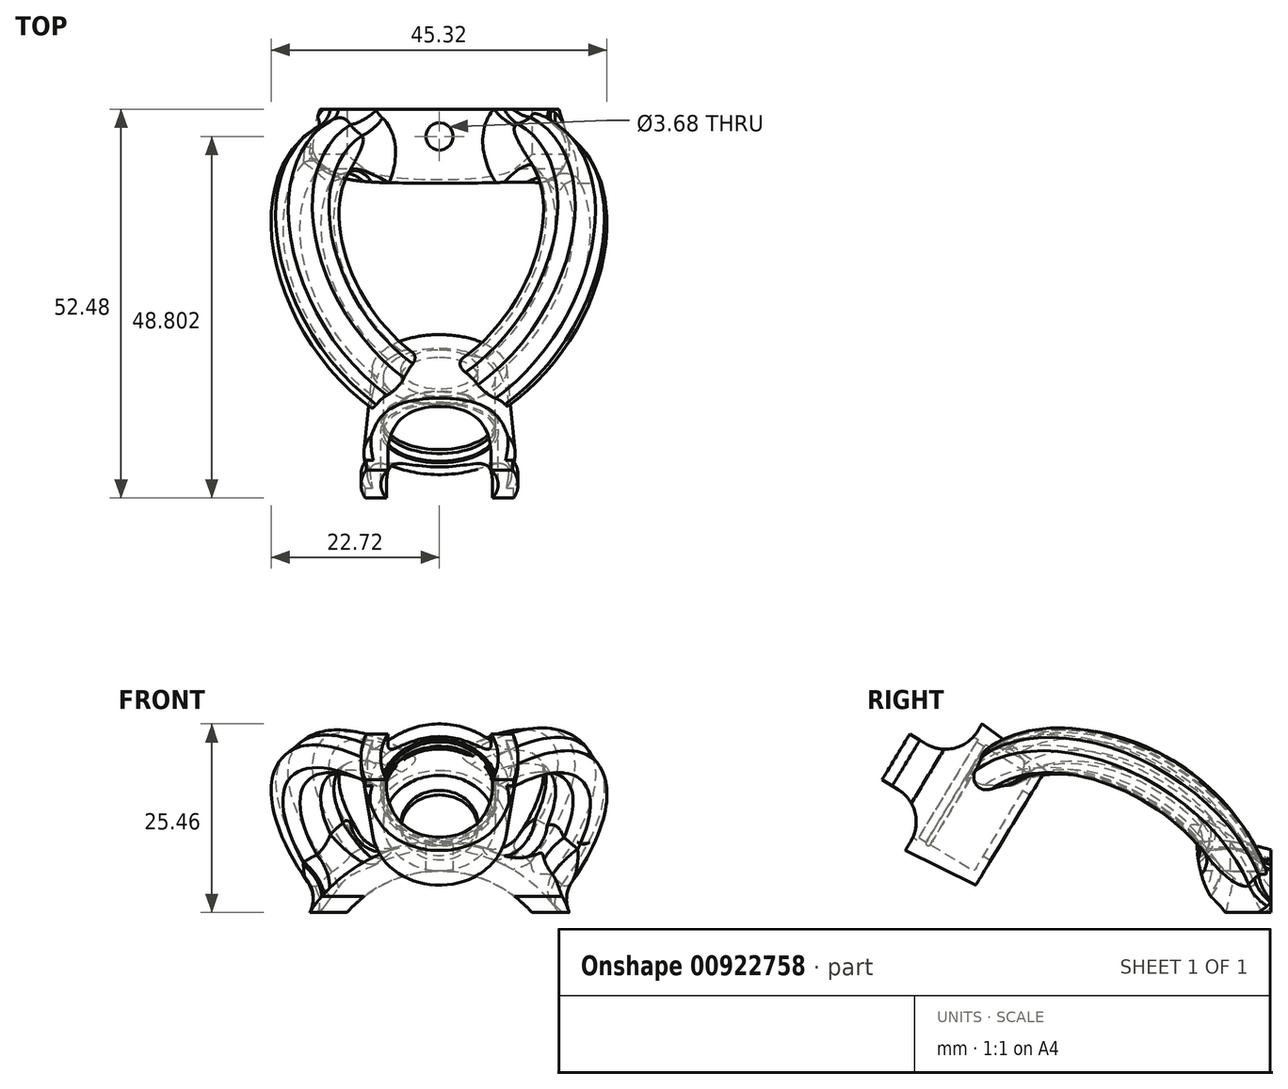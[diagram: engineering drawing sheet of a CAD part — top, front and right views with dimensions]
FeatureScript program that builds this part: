
annotation { "Feature Type Name" : "Feature", "Feature Type Description" : "" }
export const myFeature = defineFeature(function(context is Context, id is Id, definition is map)
    precondition{}
    {
        {
            var Q0;
            Q0=qCreatedBy(makeId("Right.planeOp"),FACE);
            var sketch = newSketch(context, id + "F0", { "sketchPlane" : qUnion([Q0])});
            skLineSegment(sketch, "E0", {"start": v(0, 0) * mm, "end": v(15.88, 0) * mm, "construction": true});
            skLineSegment(sketch, "E1", {"start": v(0, 0) * mm, "end": v(0, 16.68) * mm, "construction": true});
            skLineSegment(sketch, "E2", {"start": v(0, 0) * mm, "end": v(0, -16.68) * mm, "construction": true});
            skLineSegment(sketch, "E3", {"start": v(0, 16.68) * mm, "end": v(-2.38, 16.68) * mm});
            skLineSegment(sketch, "E4", {"start": v(-2.38, 16.68) * mm, "end": v(-2.38, 19.06) * mm});
            skLineSegment(sketch, "E5", {"start": v(-2.38, 19.06) * mm, "end": v(0, 19.06) * mm, "construction": true});
            skLineSegment(sketch, "E6", {"start": v(0, 19.06) * mm, "end": v(0, 16.68) * mm, "construction": true});
            skPoint(sketch, "E7", {"position": v(-12.7, 16.68) * mm});
            skLineSegment(sketch, "E8", {"start": v(-2.38, 16.68) * mm, "end": v(-12.7, 16.68) * mm});
            skLineSegment(sketch, "E9", {"start": v(-11.9, 18.96) * mm, "end": v(-11.9, 20.55) * mm});
            skPoint(sketch, "E10", {"position": v(-7.14, 20.64) * mm});
            skFitSpline(sketch, "E11", {"points": [v(0, 19.06) * mm, v(-7.14, 20.64) * mm, v(-11.9, 20.55) * mm], "startDerivative": vector(-14.9, 3.6) * mm, "endDerivative": vector(-10.3, -0.6) * mm});
            skLineSegment(sketch, "E12", {"start": v(0, 0) * mm, "end": v(-3.87, -6.39) * mm, "construction": true});
            skLineSegment(sketch, "E13", {"start": v(-3.87, -6.39) * mm, "end": v(-41.99, 16.68) * mm, "construction": true});
            skLineSegment(sketch, "E14", {"start": v(-12.7, 16.68) * mm, "end": v(-47.78, 16.68) * mm, "construction": true});
            skLineSegment(sketch, "E15", {"start": v(0, 0) * mm, "end": v(3.94, 6.52) * mm, "construction": true});
            skLineSegment(sketch, "E16", {"start": v(3.94, 6.52) * mm, "end": v(-34.18, 29.58) * mm, "construction": true});
            skLineSegment(sketch, "E17", {"start": v(-34.18, 29.58) * mm, "end": v(-41.99, 16.68) * mm, "construction": true});
            skLineSegment(sketch, "E18", {"start": v(-34.18, 29.58) * mm, "end": v(-58.62, 44.38) * mm, "construction": true});
            skLineSegment(sketch, "E19", {"start": v(-58.62, 44.38) * mm, "end": v(-66.35, 31.6) * mm, "construction": true});
            skLineSegment(sketch, "E20", {"start": v(-66.35, 31.6) * mm, "end": v(-41.99, 16.68) * mm, "construction": true});
            skLineSegment(sketch, "E21", {"start": v(-34.18, 29.58) * mm, "end": v(-35.4, 27.55) * mm});
            skLineSegment(sketch, "E22", {"start": v(-35.4, 27.55) * mm, "end": v(-34.39, 26.93) * mm});
            skLineSegment(sketch, "E23", {"start": v(-34.18, 29.58) * mm, "end": v(-41.65, 34.1) * mm});
            skLineSegment(sketch, "E24", {"start": v(-41.65, 34.1) * mm, "end": v(-40.86, 35.4) * mm});
            skLineSegment(sketch, "E25", {"start": v(-40.86, 35.4) * mm, "end": v(-32.37, 30.27) * mm});
            skLineSegment(sketch, "E26", {"start": v(-34.39, 26.93) * mm, "end": v(-32.37, 30.27) * mm});
            skLineSegment(sketch, "E27", {"start": v(-40.86, 35.4) * mm, "end": v(-47.92, 39.68) * mm});
            skLineSegment(sketch, "E28", {"start": v(-47.92, 39.68) * mm, "end": v(-48.51, 38.7) * mm});
            skLineSegment(sketch, "E29", {"start": v(-48.51, 38.7) * mm, "end": v(-41.45, 34.43) * mm});
            skLineSegment(sketch, "E30", {"start": v(-38.08, 23.13) * mm, "end": v(-42, 25.5) * mm, "construction": true});
            skLineSegment(sketch, "E31", {"start": v(-11.9, 18.96) * mm, "end": v(-7.14, 18.96) * mm});
            skLineSegment(sketch, "E32", {"start": v(-7.14, 18.96) * mm, "end": v(-4.16, 16.68) * mm});
            skLineSegment(sketch, "E33", {"start": v(-11.9, 18.96) * mm, "end": v(-11.9, 16.68) * mm});
            skLineSegment(sketch, "E34", {"start": v(-2.38, 19.06) * mm, "end": v(-2.38, 19.66) * mm});
            skLineSegment(sketch, "E35", {"start": v(-1.93, 16.68) * mm, "end": v(-1.93, 19.54) * mm});
            skLineSegment(sketch, "E36", {"start": v(-47.92, 39.68) * mm, "end": v(-47.13, 40.98) * mm});
            skLineSegment(sketch, "E37", {"start": v(-47.13, 40.98) * mm, "end": v(-45.77, 40.16) * mm});
            skLineSegment(sketch, "E38", {"start": v(-45.77, 40.16) * mm, "end": v(-46.56, 38.86) * mm});
            skCircle(sketch, "E39", {"center": v(-40.34, 33.31) * mm, "radius": 0.32 * mm});
            skLineSegment(sketch, "E40", {"start": v(-32.37, 30.27) * mm, "end": v(-43.04, 38.06) * mm});
            skLineSegment(sketch, "E41", {"start": v(-43.04, 38.06) * mm, "end": v(-43.63, 37.08) * mm});
            skLineSegment(sketch, "E42", {"start": v(-43.04, 38.06) * mm, "end": v(-46.23, 39.4) * mm});
            skSolve(sketch);
        }
        {
            var Q0;
            {var subQ0=sQuery(id+"F0.wireOp",EDGE,"41GGEf58-UM0G-m7PR-pCRU-CCuLjlQgezV2");Q0=makeQuery(id+"F0.imprint","IMPRINT",FACE,{"disambiguationData":[TD([[makeQuery(id+"F0.imprint","IMPRINT",EDGE,{"derivedFrom":subQ0}),-1.0]])]});}
            var Q1;
            {var subQ2=sQuery(id+"F0.wireOp",EDGE,"E4");Q1=makeQuery(id+"F0.imprint","IMPRINT",FACE,{"disambiguationData":[TD([[makeQuery(id+"F0.imprint","IMPRINT",EDGE,{"derivedFrom":subQ2}),1.0]])]});}
            var Q2;
            Q2=makeQuery(id+"F0.imprint","IMPRINT",FACE,{"disambiguationData":[TD([[makeQuery(id+"F0.imprint","IMPRINT",EDGE,{"derivedFrom":sQuery(id+"F0.wireOp",EDGE,"E3")}),-1.0]])]});
            var Q3;
            Q3=makeQuery(id+"F0.imprint","IMPRINT",FACE,{"disambiguationData":[TD([[makeQuery(id+"F0.imprint","IMPRINT",EDGE,{"derivedFrom":sQuery(id+"F0.wireOp",EDGE,"E31")}),-1.0]])]});
            var Q4;
            Q4=sQuery(id+"F0.wireOp",EDGE,"E0");
            revolve(context, id + "F1", {"surfaceOperationType" : NewSurfaceOperationType.NEW, "entities" : qUnion([Q0, Q1, Q2, Q3]), "axis" : qUnion([Q4]), "revolveType" : RevolveType.SYMMETRIC, "angle" : 210 * degree});
        }
        {
            var Q0;
            Q0=makeQuery(id+"F0.imprint","IMPRINT",FACE,{"disambiguationData":[TD([[makeQuery(id+"F0.imprint","IMPRINT",EDGE,{"derivedFrom":sQuery(id+"F0.wireOp",EDGE,"E21")}),1.0]])]});
            var Q1;
            {var subQ0=sQuery(id+"F0.wireOp",EDGE,"E27");Q1=makeQuery(id+"F0.imprint","IMPRINT",FACE,{"disambiguationData":[TD([[makeQuery(id+"F0.imprint","IMPRINT",EDGE,{"derivedFrom":subQ0}),1.0]])]});}
            var Q2;
            {var subQ0=sQuery(id+"F0.wireOp",EDGE,"E36");Q2=makeQuery(id+"F0.imprint","IMPRINT",FACE,{"disambiguationData":[TD([[makeQuery(id+"F0.imprint","IMPRINT",EDGE,{"derivedFrom":subQ0}),-1.0]])]});}
            var Q3;
            {var subQ0=sQuery(id+"F0.wireOp",EDGE,"E39");var subQ1=sQuery(id+"F0.wireOp",EDGE,"E23");var subQ2=makeQuery(id+"F0.imprint","INTERSECT",VERTEX,{"disambiguationData":[OD(0.0)],"derivedFrom":[subQ1,subQ0]});Q3=makeQuery(id+"F0.imprint","IMPRINT",FACE,{"disambiguationData":[TD([[makeQuery(id+"F0.imprint","IMPRINT",EDGE,{"disambiguationData":[TD([[subQ2,-1.0]])],"derivedFrom":subQ1}),-1.0]])]});}
            var Q4;
            {var subQ0=sQuery(id+"F0.wireOp",EDGE,"E39");var subQ1=sQuery(id+"F0.wireOp",EDGE,"E23");var subQ2=makeQuery(id+"F0.imprint","INTERSECT",VERTEX,{"disambiguationData":[OD(0.0)],"derivedFrom":[subQ1,subQ0]});Q4=makeQuery(id+"F0.imprint","IMPRINT",FACE,{"disambiguationData":[TD([[makeQuery(id+"F0.imprint","IMPRINT",EDGE,{"disambiguationData":[TD([[subQ2,-1.0]])],"derivedFrom":subQ1}),1.0]])]});}
            var Q5;
            {var subQ0=sQuery(id+"F0.wireOp",EDGE,"E25");Q5=makeQuery(id+"F0.imprint","IMPRINT",FACE,{"disambiguationData":[TD([[makeQuery(id+"F0.imprint","IMPRINT",EDGE,{"derivedFrom":subQ0}),1.0]])]});}
            var Q6;
            {var subQ3=sQuery(id+"F0.wireOp",EDGE,"E41");Q6=makeQuery(id+"F0.imprint","IMPRINT",FACE,{"disambiguationData":[TD([[makeQuery(id+"F0.imprint","IMPRINT",EDGE,{"derivedFrom":subQ3}),-1.0]])]});}
            var Q7;
            Q7=sQuery(id+"F0.wireOp",EDGE,"E30");
            revolve(context, id + "F2", {"operationType" : NewBodyOperationType.ADD, "surfaceOperationType" : NewSurfaceOperationType.NEW, "entities" : qUnion([Q0, Q1, Q2, Q3, Q4, Q5, Q6]), "axis" : qUnion([Q7]), "revolveType" : RevolveType.FULL});
        }
        {
            var Q0;
            Q0=makeQuery(id+"F2.opRevolve","SWEPT_FACE",FACE,{"disambiguationData":[OSD([sQuery(id+"F0.wireOp",EDGE,"E28")])]});
            var sketch = newSketch(context, id + "F3", { "sketchPlane" : qUnion([Q0])});
            skLineSegment(sketch, "E43", {"start": v(0, 0) * mm, "end": v(-5.64, 5.64) * mm, "construction": true});
            skLineSegment(sketch, "E44", {"start": v(0, 0) * mm, "end": v(0, 4.02) * mm, "construction": true});
            skLineSegment(sketch, "E45", {"start": v(0, 0) * mm, "end": v(5.64, 5.64) * mm, "construction": true});
            skLineSegment(sketch, "E46", {"start": v(0, 0) * mm, "end": v(6.46, -4.52) * mm, "construction": true});
            skLineSegment(sketch, "E47", {"start": v(0, 0) * mm, "end": v(-6.46, -4.52) * mm, "construction": true});
            skLineSegment(sketch, "E48", {"start": v(-5.64, 5.64) * mm, "end": v(-5.32, 5.96) * mm});
            skLineSegment(sketch, "E49", {"start": v(5.64, 5.64) * mm, "end": v(4.82, 6.46) * mm});
            skSolve(sketch);
        }
        {
            var Q0;
            Q0=sQuery(id+"F3.wireOp",VERTEX,"E43.end");
            var Q1;
            Q1=sQuery(id+"F3.wireOp",VERTEX,"E46.end");
            var Q2;
            Q2=qCreatedBy(makeId("Origin.pointOp"),VERTEX);
            cPlane(context, id + "F4", {"entities" : qUnion([Q0, Q1, Q2]), "cplaneType" : CPlaneType.THREE_POINT, "offset" : 25.4 * mm, "width" : 152.4 * mm, "height" : 152.4 * mm});
        }
        {
            var Q0;
            Q0=qCreatedBy(makeId("Origin.pointOp"),VERTEX);
            var Q1;
            Q1=sQuery(id+"F3.wireOp",VERTEX,"E47.end");
            var Q2;
            Q2=sQuery(id+"F3.wireOp",VERTEX,"E45.end");
            cPlane(context, id + "F5", {"entities" : qUnion([Q0, Q1, Q2]), "cplaneType" : CPlaneType.THREE_POINT, "offset" : 25.4 * mm, "width" : 152.4 * mm, "height" : 152.4 * mm});
        }
        {
            var Q0;
            Q0=makeQuery(id+"F2.opRevolve","SWEPT_FACE",FACE,{"disambiguationData":[OSD([sQuery(id+"F0.wireOp",EDGE,"E21")])]});
            var sketch = newSketch(context, id + "F6", { "sketchPlane" : qUnion([Q0])});
            skPoint(sketch, "E50.0", {"position": v(-5.64, 5.64) * mm});
            skPoint(sketch, "E50.1", {"position": v(5.64, 5.64) * mm});
            skSolve(sketch);
        }
        {
            var Q0;
            Q0=sQuery(id+"F6.wireOp",VERTEX,"E50.0");
            var Q1;
            Q1=sQuery(id+"F3.wireOp",VERTEX,"E48.end");
            var Q2;
            Q2=sQuery(id+"F3.wireOp",VERTEX,"E43.end");
            cPlane(context, id + "F7", {"entities" : qUnion([Q0, Q1, Q2]), "cplaneType" : CPlaneType.THREE_POINT, "offset" : 25.4 * mm, "width" : 152.4 * mm, "height" : 152.4 * mm});
        }
        {
            var Q0;
            Q0=sQuery(id+"F3.wireOp",VERTEX,"E49.end");
            var Q1;
            Q1=sQuery(id+"F3.wireOp",VERTEX,"E45.end");
            var Q2;
            Q2=sQuery(id+"F6.wireOp",VERTEX,"E50.1");
            cPlane(context, id + "F8", {"entities" : qUnion([Q0, Q1, Q2]), "cplaneType" : CPlaneType.THREE_POINT, "offset" : 25.4 * mm, "width" : 152.4 * mm, "height" : 152.4 * mm});
        }
        {
            var Q0;
            Q0=qCreatedBy(id+"F4.planeOp",FACE);
            var sketch = newSketch(context, id + "F9", { "sketchPlane" : qUnion([Q0])});
            skEllipse(sketch, "E51.0", {"center": v(0.37, 44.55) * mm, "majorRadius": 7.47 * mm, "minorRadius": 0.08 * mm, "majorAxis": v(-1, 0), "construction": true});
            skEllipse(sketch, "E51.1", {"center": v(0.45, 53.28) * mm, "majorRadius": 7.47 * mm, "minorRadius": 0.08 * mm, "majorAxis": v(-1, 0), "construction": true});
            skLineSegment(sketch, "E52", {"start": v(-7.17, 44.62) * mm, "end": v(-7.09, 53.35) * mm, "construction": true});
            skEllipticalArc(sketch, "E53.0", {"construction": true});
            skEllipticalArc(sketch, "E53.1", {"construction": true});
            skLineSegment(sketch, "E54", {"start": v(-15, 17.76) * mm, "end": v(23.12, 2.43) * mm, "construction": true});
            skArc(sketch, "E55", {"start": v(-7.13, 48.99) * mm, "mid": v(-22.85, 23.4) * mm, "end": v(4.06, 10.1) * mm, "construction": true});
            skArc(sketch, "E56", {"start": v(-7.13, 48.99) * mm, "mid": v(-23.25, 33.02) * mm, "end": v(-14.53, 12.07) * mm});
            skLineSegment(sketch, "E57", {"start": v(-12.93, 11.43) * mm, "end": v(-12.93, 11.43) * mm});
            const initialGuessF9  = {"E53.0": [0.004051244934595459, 0.010101059482229056, -0.9281334338456237, 0.37224767155474775, 0.02064385, 0.008372044976106609, 3.659643135564051, 1.041649257572556], "E53.1": [0.004051244934595459, 0.010101059482229056, 0.9281334338456237, -0.37224767155474775, 0.02064385, 0.008372044976106609, 0.5180504819742582, 4.18324191116235]};
            skSetInitialGuess(sketch, initialGuessF9);
            skSolve(sketch);
        }
        {
            var Q0;
            Q0=qCreatedBy(id+"F7.planeOp",FACE);
            var sketch = newSketch(context, id + "F10", { "sketchPlane" : qUnion([Q0])});
            skPoint(sketch, "E58.0", {"position": v(45.01, 19.14) * mm});
            skCircle(sketch, "E59", {"center": v(45.01, 19.14) * mm, "radius": 3.05 * mm});
            skCircle(sketch, "E60", {"center": v(42.38, 20.68) * mm, "radius": 1.65 * mm});
            skCircle(sketch, "E61", {"center": v(47.5, 17.38) * mm, "radius": 1.7 * mm});
            skSolve(sketch);
        }
        {
            var Q0;
            Q0=qSketchRegion(id+"F10",true);
            var Q1;
            Q1=sQuery(id+"F9.wireOp",EDGE,"E56");
            sweep(context, id + "F11", {"operationType" : NewBodyOperationType.ADD, "profiles" : qUnion([Q0]), "path" : qUnion([Q1])});
        }
        {
            var Q0;
            Q0=qCreatedBy(id+"F5.planeOp",FACE);
            var sketch = newSketch(context, id + "F12", { "sketchPlane" : qUnion([Q0])});
            skEllipse(sketch, "E62.0", {"center": v(-0.37, 44.55) * mm, "majorRadius": 7.54 * mm, "minorRadius": 0.09 * mm, "majorAxis": v(-1, 0), "construction": true});
            skEllipse(sketch, "E62.1", {"center": v(-0.45, 53.28) * mm, "majorRadius": 7.54 * mm, "minorRadius": 0.09 * mm, "majorAxis": v(-1, 0), "construction": true});
            skEllipticalArc(sketch, "E63.0", {"construction": true});
            skEllipticalArc(sketch, "E63.1", {"construction": true});
            skLineSegment(sketch, "E64", {"start": v(15, 17.76) * mm, "end": v(15, 17.76) * mm});
            skPoint(sketch, "E65.startSnap0", {"position": v(7.09, 53.35) * mm});
            skArc(sketch, "E66", {"start": v(16.15, 13.17) * mm, "mid": v(23.08, 34.45) * mm, "end": v(6.25, 49.2) * mm, "construction": true});
            skArc(sketch, "E67", {"start": v(14.48, 11.97) * mm, "mid": v(23.37, 33.27) * mm, "end": v(6.61, 49.14) * mm});
            skLineSegment(sketch, "E68", {"start": v(14.6, 13.91) * mm, "end": v(14.6, 13.91) * mm});
            const initialGuessF12  = {"E63.0": [-0.004060244768928434, 0.010094771245792443, 0.9277671316692641, 0.3731596835058503, 0.020548599999999997, 0.008343060637084959, 5.240693512241937, 2.6226996342504427], "E63.1": [-0.004060244768928434, 0.010094771245792443, -0.9277671316692641, -0.3731596835058503, 0.020548599999999997, 0.008343060637084959, 2.0991008586521445, 5.764292287840235]};
            skSetInitialGuess(sketch, initialGuessF12);
            skSolve(sketch);
        }
        {
            var Q0;
            Q0=qCreatedBy(id+"F8.planeOp",FACE);
            var sketch = newSketch(context, id + "F13", { "sketchPlane" : qUnion([Q0])});
            skPoint(sketch, "E69.0", {"position": v(45.18, 19.3) * mm});
            skCircle(sketch, "E70", {"center": v(45.18, 19.3) * mm, "radius": 3.05 * mm});
            skCircle(sketch, "E71", {"center": v(43.13, 21.55) * mm, "radius": 1.68 * mm});
            skCircle(sketch, "E72", {"center": v(47.06, 16.9) * mm, "radius": 1.8 * mm});
            skSolve(sketch);
        }
        {
            var Q0;
            Q0=qSketchRegion(id+"F13",true);
            var Q1;
            Q1=sQuery(id+"F12.wireOp",EDGE,"E67");
            sweep(context, id + "F14", {"operationType" : NewBodyOperationType.ADD, "profiles" : qUnion([Q0]), "path" : qUnion([Q1])});
        }
        {
            var Q0;
            Q0=qCreatedBy(makeId("Top.planeOp"),FACE);
            var sketch = newSketch(context, id + "F15", { "sketchPlane" : qUnion([Q0])});
            skCircle(sketch, "E73", {"center": v(0, -5.6) * mm, "radius": 1.84 * mm});
            skSolve(sketch);
        }
        {
            var Q0;
            Q0=qSketchRegion(id+"F15",true);
            extrude(context, id + "F16", {"entities" : qUnion([Q0]), "operationType" : NewBodyOperationType.REMOVE, "depth" : 25.4 * mm, "offsetDistance" : 25.4 * mm});
        }
        {
            var Q0;
            Q0=qCreatedBy(makeId("Right.planeOp"),FACE);
            var sketch = newSketch(context, id + "F17", { "sketchPlane" : qUnion([Q0])});
            skLineSegment(sketch, "E74.0", {"start": v(-1.93, -5.06) * mm, "end": v(-1.93, 19.54) * mm});
            skLineSegment(sketch, "E74.1", {"start": v(-11.9, -5.32) * mm, "end": v(-11.9, 20.55) * mm});
            skFitSpline(sketch, "E74.2", {"points": [v(0, -4.93) * mm, v(-2.75, -5.1) * mm, v(-6.92, -5.44) * mm, v(-10.37, -5.34) * mm, v(-11.9, -5.32) * mm]});
            skPoint(sketch, "E74.3", {"position": v(-6.86, -5.34) * mm});
            skFitSpline(sketch, "E75", {"points": [v(-11.9, 14.76) * mm, v(-5.13, 6) * mm, v(-4.15, -1.1) * mm], "startDerivative": vector(17.52, -12.27) * mm, "endDerivative": vector(0.53, -18.23) * mm});
            skLineSegment(sketch, "E76", {"start": v(-4.15, -1.1) * mm, "end": v(-3.68, -5.17) * mm});
            skFitSpline(sketch, "E77", {"points": [v(-9.41, 12.62) * mm, v(-11.41, 16.58) * mm, v(-11.9, 20.55) * mm], "startDerivative": vector(-5.24, 3.22) * mm, "endDerivative": vector(-0.07, 8) * mm});
            skPoint(sketch, "E78.start.orphan", {"position": v(-6.92, 7.75) * mm});
            skLineSegment(sketch, "E79", {"start": v(-11.9, 19.25) * mm, "end": v(-19.7, 19.25) * mm});
            skLineSegment(sketch, "E80", {"start": v(-19.7, 19.25) * mm, "end": v(-19.7, -5.77) * mm});
            skLineSegment(sketch, "E81", {"start": v(-19.7, -5.77) * mm, "end": v(-3.7, -5.77) * mm});
            skLineSegment(sketch, "E82", {"start": v(-3.7, -5.77) * mm, "end": v(-3.68, -5.17) * mm});
            skSolve(sketch);
        }
        {
            var Q0;
            Q0=makeQuery(id+"F17.imprint","IMPRINT",FACE,{"disambiguationData":[TD([[makeQuery(id+"F17.imprint","IMPRINT",EDGE,{"derivedFrom":sQuery(id+"F17.wireOp",EDGE,"E75")}),-1.0]])]});
            var Q1;
            {var subQ0=sQuery(id+"F17.wireOp",EDGE,"E80");Q1=makeQuery(id+"F17.imprint","IMPRINT",FACE,{"disambiguationData":[TD([[makeQuery(id+"F17.imprint","IMPRINT",EDGE,{"derivedFrom":subQ0}),1.0]])]});}
            var Q2;
            Q2=makeQuery(id+"F17.imprint","IMPRINT",FACE,{"disambiguationData":[TD([[makeQuery(id+"F17.imprint","IMPRINT",EDGE,{"derivedFrom":sQuery(id+"F17.wireOp",EDGE,"b1ca824d-34d5-41d4-adb1-23ad9cf70987")}),-1.0]])]});
            extrude(context, id + "F18", {"entities" : qUnion([Q0, Q1, Q2]), "operationType" : NewBodyOperationType.REMOVE, "endBound" : BoundingType.SYMMETRIC, "oppositeDirection" : true, "depth" : 81.28 * mm, "offsetDistance" : 25.4 * mm});
        }
        {
            var Q0;
            Q0=qSketchRegion(id+"F17",true);
            extrude(context, id + "F19", {"entities" : qUnion([Q0]), "operationType" : NewBodyOperationType.REMOVE, "endBound" : BoundingType.SYMMETRIC, "oppositeDirection" : true, "depth" : 54.36 * mm, "offsetDistance" : 25.4 * mm});
        }
        {
            var Q0;
            Q0=qCreatedBy(makeId("Front.planeOp"),FACE);
            var sketch = newSketch(context, id + "F20", { "sketchPlane" : qUnion([Q0])});
            skLineSegment(sketch, "E83", {"start": v(-19.88, 11.06) * mm, "end": v(23.14, 11.06) * mm});
            skLineSegment(sketch, "E84", {"start": v(23.14, 11.06) * mm, "end": v(23.14, -5.4) * mm});
            skLineSegment(sketch, "E85", {"start": v(23.14, -5.4) * mm, "end": v(-21.35, -5.4) * mm});
            skLineSegment(sketch, "E86", {"start": v(-21.35, -5.4) * mm, "end": v(-19.88, 11.06) * mm});
            skSolve(sketch);
        }
        {
            var Q0;
            Q0=makeQuery(id+"F20.imprint","IMPRINT",FACE,{"disambiguationData":[TD([[makeQuery(id+"F20.imprint","IMPRINT",EDGE,{"derivedFrom":sQuery(id+"F20.wireOp",EDGE,"E83")}),-1.0]])]});
            extrude(context, id + "F21", {"entities" : qUnion([Q0]), "operationType" : NewBodyOperationType.REMOVE, "endBound" : BoundingType.SYMMETRIC, "oppositeDirection" : true, "depth" : 50.8 * mm, "offsetDistance" : 25.4 * mm});
        }
        {
            var Q0;
            {var subQ0=sQuery(id+"F13.wireOp",EDGE,"E72");var subQ1=sQuery(id+"F13.wireOp",EDGE,"E70");var subQ2=sQuery(id+"F12.wireOp",EDGE,"E67");Q0=makeQuery(id+"F14.opSweep","SWEPT_EDGE",EDGE,{"disambiguationData":[OSD([subQ2,subQ1,subQ0]),TDD([subQ2,makeQuery(id+"F13.imprint","INTERSECT",VERTEX,{"disambiguationData":[OD(1.0)],"derivedFrom":[subQ1,subQ0]})])]});}
            var Q1;
            {var subQ0=sQuery(id+"F13.wireOp",EDGE,"E71");var subQ1=sQuery(id+"F13.wireOp",EDGE,"E70");var subQ2=sQuery(id+"F12.wireOp",EDGE,"E67");Q1=makeQuery(id+"F14.opSweep","SWEPT_EDGE",EDGE,{"disambiguationData":[OSD([subQ2,subQ1,subQ0]),TDD([subQ2,makeQuery(id+"F13.imprint","INTERSECT",VERTEX,{"disambiguationData":[OD(1.0)],"derivedFrom":[subQ1,subQ0]})])]});}
            var Q2;
            {var subQ0=sQuery(id+"F10.wireOp",EDGE,"E60");var subQ1=sQuery(id+"F10.wireOp",EDGE,"E59");var subQ2=sQuery(id+"F9.wireOp",EDGE,"E56");Q2=makeQuery(id+"F11.opSweep","SWEPT_EDGE",EDGE,{"disambiguationData":[OSD([subQ2,subQ1,subQ0]),TDD([subQ2,makeQuery(id+"F10.imprint","INTERSECT",VERTEX,{"disambiguationData":[OD(1.0)],"derivedFrom":[subQ1,subQ0]})])]});}
            var Q3;
            {var subQ0=sQuery(id+"F10.wireOp",EDGE,"E61");var subQ1=sQuery(id+"F10.wireOp",EDGE,"E59");var subQ2=sQuery(id+"F9.wireOp",EDGE,"E56");Q3=makeQuery(id+"F11.opSweep","SWEPT_EDGE",EDGE,{"disambiguationData":[OSD([subQ2,subQ1,subQ0]),TDD([subQ2,makeQuery(id+"F10.imprint","INTERSECT",VERTEX,{"disambiguationData":[OD(1.0)],"derivedFrom":[subQ1,subQ0]})])]});}
            var Q4;
            {var subQ0=sQuery(id+"F10.wireOp",EDGE,"E61");var subQ1=sQuery(id+"F10.wireOp",EDGE,"E59");var subQ2=sQuery(id+"F9.wireOp",EDGE,"E56");Q4=makeQuery(id+"F11.opSweep","SWEPT_EDGE",EDGE,{"disambiguationData":[OSD([subQ2,subQ1,subQ0]),TDD([subQ2,makeQuery(id+"F10.imprint","INTERSECT",VERTEX,{"disambiguationData":[OD(0.0)],"derivedFrom":[subQ1,subQ0]})])]});}
            var Q5;
            {var subQ0=sQuery(id+"F10.wireOp",EDGE,"E60");var subQ1=sQuery(id+"F10.wireOp",EDGE,"E59");var subQ2=sQuery(id+"F9.wireOp",EDGE,"E56");Q5=makeQuery(id+"F11.opSweep","SWEPT_EDGE",EDGE,{"disambiguationData":[OSD([subQ2,subQ1,subQ0]),TDD([subQ2,makeQuery(id+"F10.imprint","INTERSECT",VERTEX,{"disambiguationData":[OD(0.0)],"derivedFrom":[subQ1,subQ0]})])]});}
            var Q6;
            {var subQ0=sQuery(id+"F13.wireOp",EDGE,"E71");var subQ1=sQuery(id+"F13.wireOp",EDGE,"E70");var subQ2=sQuery(id+"F12.wireOp",EDGE,"E67");Q6=makeQuery(id+"F14.opSweep","SWEPT_EDGE",EDGE,{"disambiguationData":[OSD([subQ2,subQ1,subQ0]),TDD([subQ2,makeQuery(id+"F13.imprint","INTERSECT",VERTEX,{"disambiguationData":[OD(0.0)],"derivedFrom":[subQ1,subQ0]})])]});}
            var Q7;
            {var subQ0=sQuery(id+"F13.wireOp",EDGE,"E72");var subQ1=sQuery(id+"F13.wireOp",EDGE,"E70");var subQ2=sQuery(id+"F12.wireOp",EDGE,"E67");Q7=makeQuery(id+"F14.opSweep","SWEPT_EDGE",EDGE,{"disambiguationData":[OSD([subQ2,subQ1,subQ0]),TDD([subQ2,makeQuery(id+"F13.imprint","INTERSECT",VERTEX,{"disambiguationData":[OD(0.0)],"derivedFrom":[subQ1,subQ0]})])]});}
            fillet(context, id + "F22", {"entities" : qUnion([Q0, Q1, Q2, Q3, Q4, Q5, Q6, Q7]), "tangentPropagation" : true, "radius" : 15.24 * mm, "defaultsChanged" : true, "vertexSettings" : [], "allowEdgeOverflow" : false});
        }
        {
            var Q0;
            Q0=makeQuery(id+"F2.opRevolve","SWEPT_FACE",FACE,{"disambiguationData":[OSD([sQuery(id+"F0.wireOp",EDGE,"E28"),sQuery(id+"F0.wireOp",EDGE,"E36")])]});
            var sketch = newSketch(context, id + "F23", { "sketchPlane" : qUnion([Q0])});
            skLineSegment(sketch, "E87", {"start": v(-26.95, 3.85) * mm, "end": v(32.6, 3.85) * mm});
            skLineSegment(sketch, "E88", {"start": v(-27.36, -3.39) * mm, "end": v(29.87, -3.39) * mm});
            skLineSegment(sketch, "E89", {"start": v(32.6, 3.85) * mm, "end": v(28.19, 12.58) * mm});
            skLineSegment(sketch, "E90", {"start": v(28.19, 12.58) * mm, "end": v(-20.79, 12.58) * mm});
            skLineSegment(sketch, "E91", {"start": v(-20.79, 12.58) * mm, "end": v(-26.95, 3.85) * mm});
            skLineSegment(sketch, "E92", {"start": v(-27.36, -3.39) * mm, "end": v(-16.8, -13.2) * mm});
            skLineSegment(sketch, "E93", {"start": v(-16.8, -13.2) * mm, "end": v(19.3, -15.86) * mm});
            skLineSegment(sketch, "E94", {"start": v(19.3, -15.86) * mm, "end": v(29.87, -3.39) * mm});
            skSolve(sketch);
        }
        {
            var Q0;
            Q0 = qSketchRegion(id + "F23", true);
            extrude(context, id + "F24", {"entities" : qUnion([Q0]), "operationType" : NewBodyOperationType.REMOVE, "oppositeDirection" : true, "depth" : 7.62 * mm, "offsetDistance" : 25.4 * mm});
        }
        {
            var Q0;
            Q0=makeQuery(id+"F24.boolean.opBoolean","COPY",EDGE,{"disambiguationData":[OD(0.0)],"derivedFrom":makeQuery(id+"F24.opExtrude","CAP_EDGE",EDGE,{"disambiguationData":[OSD([sQuery(id+"F23.wireOp",EDGE,"E87")])],"isStart":false})});
            var Q1;
            Q1=makeQuery(id+"F24.boolean.opBoolean","COPY",EDGE,{"disambiguationData":[OD(1.0)],"derivedFrom":makeQuery(id+"F24.opExtrude","CAP_EDGE",EDGE,{"disambiguationData":[OSD([sQuery(id+"F23.wireOp",EDGE,"E87")])],"isStart":false})});
            var Q2;
            Q2=makeQuery(id+"F24.boolean.opBoolean","COPY",EDGE,{"disambiguationData":[OD(1.0)],"derivedFrom":makeQuery(id+"F24.opExtrude","CAP_EDGE",EDGE,{"disambiguationData":[OSD([sQuery(id+"F23.wireOp",EDGE,"E88")])],"isStart":false})});
            var Q3;
            Q3=makeQuery(id+"F24.boolean.opBoolean","COPY",EDGE,{"disambiguationData":[OD(0.0)],"derivedFrom":makeQuery(id+"F24.opExtrude","CAP_EDGE",EDGE,{"disambiguationData":[OSD([sQuery(id+"F23.wireOp",EDGE,"E88")])],"isStart":false})});
            fillet(context, id + "F25", {"entities" : qUnion([Q0, Q1, Q2, Q3]), "tangentPropagation" : true, "radius" : 5.08 * mm, "defaultsChanged" : true, "vertexSettings" : [], "allowEdgeOverflow" : false});
        }
        {
            var Q0;
            Q0=makeQuery(id+"F24.boolean.opBoolean","COPY",FACE,{"derivedFrom":makeQuery(id+"F24.opExtrude","CAP_FACE",FACE,{"disambiguationData":[OSD([sQuery(id+"F23.wireOp",EDGE,"E88"),sQuery(id+"F23.wireOp",EDGE,"E92"),sQuery(id+"F23.wireOp",EDGE,"E93"),sQuery(id+"F23.wireOp",EDGE,"E94")])],"isStart":false})});
            var sketch = newSketch(context, id + "F26", { "sketchPlane" : qUnion([Q0])});
            skCircle(sketch, "E95.0", {"center": v(0, 0.08) * mm, "radius": 7.54 * mm});
            skLineSegment(sketch, "E96", {"start": v(-7.3, 2) * mm, "end": v(7.3, 2) * mm});
            skSolve(sketch);
        }
        {
            var Q0;
            {var subQ0=sQuery(id+"F26.wireOp",EDGE,"E96");Q0=makeQuery(id+"F26.imprint","IMPRINT",FACE,{"disambiguationData":[TD([[makeQuery(id+"F26.imprint","IMPRINT",EDGE,{"derivedFrom":subQ0}),1.0]])]});}
            extrude(context, id + "F27", {"entities" : qUnion([Q0]), "operationType" : NewBodyOperationType.REMOVE, "oppositeDirection" : true, "depth" : 7.85 * mm, "offsetDistance" : 25.4 * mm});
        }
        {
            var Q0;
            {var subQ0=sQuery(id+"F13.wireOp",EDGE,"E70");var subQ1=sQuery(id+"F12.wireOp",EDGE,"E67");Q0=makeQuery(id+"F14.boolean.opBoolean","INTERSECT",EDGE,{"derivedFrom":[makeQuery(id+"F1.opRevolve","SWEPT_FACE",FACE,{"disambiguationData":[OSD([sQuery(id+"F0.wireOp",EDGE,"E11")])]}),makeQuery(id+"F14.opSweep","SWEPT_FACE",FACE,{"disambiguationData":[OSD([subQ1,subQ0]),TDD([subQ1,makeQuery(id+"F13.imprint","IMPRINT",EDGE,{"disambiguationData":[TD([[makeQuery(id+"F13.imprint","INTERSECT",VERTEX,{"disambiguationData":[OD(1.0)],"derivedFrom":[subQ0,sQuery(id+"F13.wireOp",EDGE,"E71")]}),1.0]])],"derivedFrom":subQ0})])]})]});}
            var Q1;
            {var subQ0=sQuery(id+"F10.wireOp",EDGE,"E59");var subQ1=sQuery(id+"F9.wireOp",EDGE,"E56");Q1=makeQuery(id+"F11.boolean.opBoolean","INTERSECT",EDGE,{"derivedFrom":[makeQuery(id+"F1.opRevolve","SWEPT_FACE",FACE,{"disambiguationData":[OSD([sQuery(id+"F0.wireOp",EDGE,"E11")])]}),makeQuery(id+"F11.opSweep","SWEPT_FACE",FACE,{"disambiguationData":[OSD([subQ1,subQ0]),TDD([subQ1,makeQuery(id+"F10.imprint","IMPRINT",EDGE,{"disambiguationData":[TD([[makeQuery(id+"F10.imprint","INTERSECT",VERTEX,{"disambiguationData":[OD(1.0)],"derivedFrom":[subQ0,sQuery(id+"F10.wireOp",EDGE,"E60")]}),1.0]])],"derivedFrom":subQ0})])]})]});}
            var Q2;
            {var subQ0=sQuery(id+"F10.wireOp",EDGE,"E59");var subQ1=sQuery(id+"F9.wireOp",EDGE,"E56");Q2=makeQuery(id+"F11.boolean.opBoolean","INTERSECT",EDGE,{"derivedFrom":[makeQuery(id+"F2.opRevolve","SWEPT_FACE",FACE,{"disambiguationData":[OSD([sQuery(id+"F0.wireOp",EDGE,"E25"),sQuery(id+"F0.wireOp",EDGE,"E27")])]}),makeQuery(id+"F11.opSweep","SWEPT_FACE",FACE,{"disambiguationData":[OSD([subQ1,subQ0]),TDD([subQ1,makeQuery(id+"F10.imprint","IMPRINT",EDGE,{"disambiguationData":[TD([[makeQuery(id+"F10.imprint","INTERSECT",VERTEX,{"disambiguationData":[OD(1.0)],"derivedFrom":[subQ0,sQuery(id+"F10.wireOp",EDGE,"E60")]}),1.0]])],"derivedFrom":subQ0})])]})]});}
            var Q3;
            {var subQ0=sQuery(id+"F13.wireOp",EDGE,"E70");var subQ1=sQuery(id+"F12.wireOp",EDGE,"E67");Q3=makeQuery(id+"F14.boolean.opBoolean","INTERSECT",EDGE,{"derivedFrom":[makeQuery(id+"F2.opRevolve","SWEPT_FACE",FACE,{"disambiguationData":[OSD([sQuery(id+"F0.wireOp",EDGE,"E25"),sQuery(id+"F0.wireOp",EDGE,"E27")])]}),makeQuery(id+"F14.opSweep","SWEPT_FACE",FACE,{"disambiguationData":[OSD([subQ1,subQ0]),TDD([subQ1,makeQuery(id+"F13.imprint","IMPRINT",EDGE,{"disambiguationData":[TD([[makeQuery(id+"F13.imprint","INTERSECT",VERTEX,{"disambiguationData":[OD(1.0)],"derivedFrom":[subQ0,sQuery(id+"F13.wireOp",EDGE,"E71")]}),1.0]])],"derivedFrom":subQ0})])]})]});}
            fillet(context, id + "F28", {"entities" : qUnion([Q0, Q1, Q2, Q3]), "tangentPropagation" : true, "radius" : 4.32 * mm, "defaultsChanged" : true, "vertexSettings" : [], "allowEdgeOverflow" : false});
        }
    });
